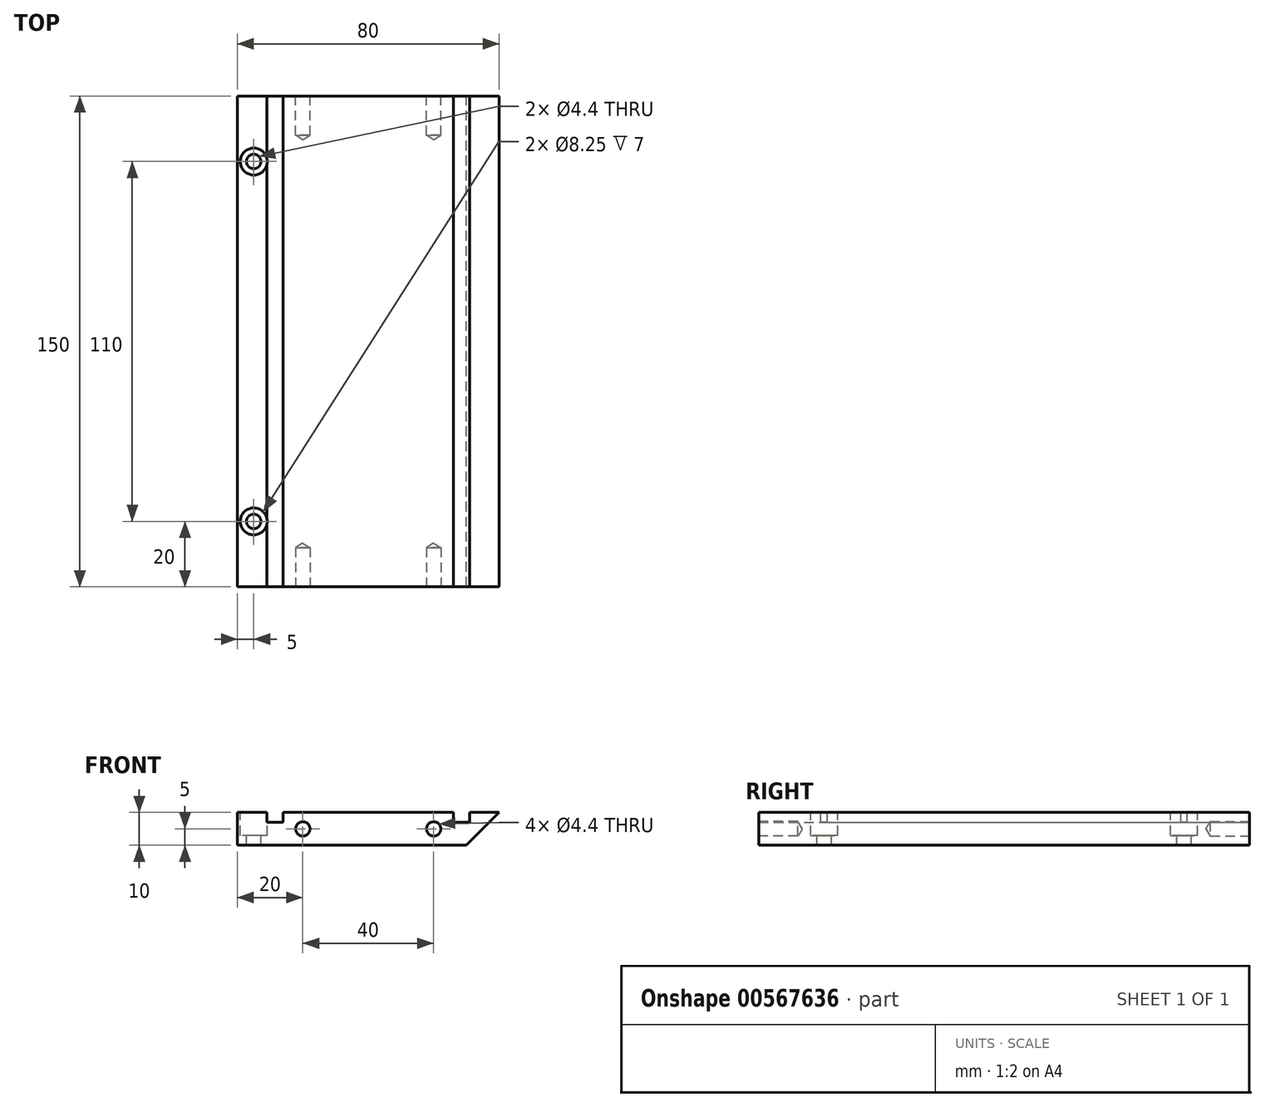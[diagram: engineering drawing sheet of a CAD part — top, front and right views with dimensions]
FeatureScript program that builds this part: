
annotation { "Feature Type Name" : "Feature", "Feature Type Description" : "" }
export const myFeature = defineFeature(function(context is Context, id is Id, definition is map)
    precondition{}
    {
        {
            var Q0;
            Q0=qCreatedBy(makeId("Front.planeOp"),FACE);
            var sketch = newSketch(context, id + "F0", { "sketchPlane" : qUnion([Q0])});
            skLineSegment(sketch, "E0.left", {"start": v(0, 0) * mm, "end": v(0, 10) * mm});
            skLineSegment(sketch, "E1", {"start": v(0, 10) * mm, "end": v(80, 10) * mm});
            skLineSegment(sketch, "E2", {"start": v(80, 10) * mm, "end": v(70, 0) * mm});
            skLineSegment(sketch, "E3", {"start": v(70, 0) * mm, "end": v(0, 0) * mm});
            skSolve(sketch);
        }
        {
            var Q0;
            Q0 = qSketchRegion(id + "F0", true);
            extrude(context, id + "F1", {"entities" : qUnion([Q0]), "depth" : 150 * mm, "offsetDistance" : 25 * mm});
        }
        {
            var Q0;
            Q0=makeQuery(id+"F1.opExtrude","CAP_FACE",FACE,{"disambiguationData":[OSD([sQuery(id+"F0.wireOp",EDGE,"E0.bottom"),sQuery(id+"F0.wireOp",EDGE,"E0.top"),sQuery(id+"F0.wireOp",EDGE,"E0.left"),sQuery(id+"F0.wireOp",EDGE,"E0.right")])],"isStart":false});
            var sketch = newSketch(context, id + "F2", { "sketchPlane" : qUnion([Q0])});
            skLineSegment(sketch, "E4", {"start": v(0, 5) * mm, "end": v(20, 5) * mm});
            skLineSegment(sketch, "E5", {"start": v(20, 5) * mm, "end": v(20, 10) * mm});
            skLineSegment(sketch, "E6", {"start": v(60, 10) * mm, "end": v(60, 5) * mm});
            skSolve(sketch);
        }
        {
            var Q0;
            Q0=sQuery(id+"F2.wireOp",VERTEX,"E5.start");
            var Q1;
            Q1=sQuery(id+"F2.wireOp",VERTEX,"E6.end");
            var Q2;
            Q2=makeQuery(id+"F1.opExtrude","SWEPT_BODY",BODY,{"disambiguationData":[OSD([sQuery(id+"F0.wireOp",EDGE,"E0.bottom"),sQuery(id+"F0.wireOp",EDGE,"E0.top"),sQuery(id+"F0.wireOp",EDGE,"E0.left"),sQuery(id+"F0.wireOp",EDGE,"E0.right")])]});
            hole(context, id + "F3", {"style" : HoleStyle.SIMPLE, "endStyle" : HoleEndStyle.BLIND, "standardTappedOrClearance" : lookupTablePath({ "standard" : "ISO", "fit" : "Normal", "size" : "M4", "type" : "Clearance" }), "standardBlindInLast" : lookupTablePath({ "fit" : "Standard", "standard" : "ISO", "size" : "M4", "type" : "Clearance" }), "holeDiameter" : 4.4 * mm, "holeDepth" : 12 * mm, "isTappedThrough" : true, "tappedDepth" : 12 * mm, "tapClearance" : 3, "locations" : qUnion([Q0, Q1]), "scope" : qUnion([Q2])});
        }
        {
            var Q0;
            Q0=makeQuery(id+"F1.opExtrude","CAP_FACE",FACE,{"disambiguationData":[OSD([sQuery(id+"F0.wireOp",EDGE,"E0.bottom"),sQuery(id+"F0.wireOp",EDGE,"E0.top"),sQuery(id+"F0.wireOp",EDGE,"E0.left"),sQuery(id+"F0.wireOp",EDGE,"E0.right")])],"isStart":true});
            var sketch = newSketch(context, id + "F4", { "sketchPlane" : qUnion([Q0])});
            skLineSegment(sketch, "E7", {"start": v(-60, 10) * mm, "end": v(-60, 5) * mm});
            skLineSegment(sketch, "E8", {"start": v(-20, 10) * mm, "end": v(-20, 5) * mm});
            skSolve(sketch);
        }
        {
            var Q0;
            Q0=sQuery(id+"F4.wireOp",VERTEX,"E7.end");
            var Q1;
            Q1=sQuery(id+"F4.wireOp",VERTEX,"E8.end");
            var Q2;
            Q2=makeQuery(id+"F1.opExtrude","SWEPT_BODY",BODY,{"disambiguationData":[OSD([sQuery(id+"F0.wireOp",EDGE,"E0.bottom"),sQuery(id+"F0.wireOp",EDGE,"E0.top"),sQuery(id+"F0.wireOp",EDGE,"E0.left"),sQuery(id+"F0.wireOp",EDGE,"E0.right")])]});
            hole(context, id + "F5", {"style" : HoleStyle.SIMPLE, "endStyle" : HoleEndStyle.BLIND, "standardTappedOrClearance" : lookupTablePath({ "standard" : "ISO", "fit" : "Normal", "size" : "M4", "type" : "Clearance" }), "standardBlindInLast" : lookupTablePath({ "fit" : "Standard", "standard" : "ISO", "size" : "M4", "type" : "Clearance" }), "holeDiameter" : 4.4 * mm, "holeDepth" : 12 * mm, "isTappedThrough" : true, "tappedDepth" : 12 * mm, "tapClearance" : 3, "locations" : qUnion([Q0, Q1]), "scope" : qUnion([Q2])});
        }
        {
            var Q0;
            Q0=makeQuery(id+"F1.opExtrude","CAP_FACE",FACE,{"disambiguationData":[OSD([sQuery(id+"F0.wireOp",EDGE,"E0.bottom"),sQuery(id+"F0.wireOp",EDGE,"E0.top"),sQuery(id+"F0.wireOp",EDGE,"E0.left"),sQuery(id+"F0.wireOp",EDGE,"E0.right")])],"isStart":true});
            var sketch = newSketch(context, id + "F6", { "sketchPlane" : qUnion([Q0])});
            skLineSegment(sketch, "E9.bottom", {"start": v(-71, 10) * mm, "end": v(-66, 10) * mm});
            skLineSegment(sketch, "E9.top", {"start": v(-71, 7) * mm, "end": v(-66, 7) * mm});
            skLineSegment(sketch, "E9.left", {"start": v(-71, 10) * mm, "end": v(-71, 7) * mm});
            skLineSegment(sketch, "E9.right", {"start": v(-66, 10) * mm, "end": v(-66, 7) * mm});
            skLineSegment(sketch, "E10.bottom", {"start": v(-14, 10) * mm, "end": v(-9, 10) * mm});
            skLineSegment(sketch, "E10.top", {"start": v(-14, 7) * mm, "end": v(-9, 7) * mm});
            skLineSegment(sketch, "E10.left", {"start": v(-14, 10) * mm, "end": v(-14, 7) * mm});
            skLineSegment(sketch, "E10.right", {"start": v(-9, 10) * mm, "end": v(-9, 7) * mm});
            skSolve(sketch);
        }
        {
            var Q0;
            Q0 = qSketchRegion(id + "F6", true);
            extrude(context, id + "F7", {"entities" : qUnion([Q0]), "operationType" : NewBodyOperationType.REMOVE, "endBound" : BoundingType.UP_TO_NEXT, "oppositeDirection" : true, "depth" : 25 * mm, "offsetDistance" : 25 * mm});
        }
        {
            var Q0;
            {var subQ0=sQuery(id+"F0.wireOp",EDGE,"E0.left");var subQ3=sQuery(id+"F0.wireOp",EDGE,"E1");Q0=makeQuery(id+"F7.boolean.opBoolean","SPLIT",FACE,{"disambiguationData":[TD([makeQuery(id+"F1.opExtrude","SWEPT_FACE",FACE,{"disambiguationData":[OSD([subQ0])]})])],"derivedFrom":makeQuery(id+"F1.opExtrude","SWEPT_FACE",FACE,{"disambiguationData":[OSD([subQ3])]})});}
            var sketch = newSketch(context, id + "F8", { "sketchPlane" : qUnion([Q0])});
            skLineSegment(sketch, "E11", {"start": v(5, -150) * mm, "end": v(5, -130) * mm});
            skLineSegment(sketch, "E12", {"start": v(5, 0) * mm, "end": v(5, -20) * mm});
            skSolve(sketch);
        }
        {
            var Q0;
            Q0=sQuery(id+"F8.wireOp",VERTEX,"E11.end");
            var Q1;
            Q1=sQuery(id+"F8.wireOp",VERTEX,"E12.end");
            var Q2;
            Q2=makeQuery(id+"F1.opExtrude","SWEPT_BODY",BODY,{"disambiguationData":[OSD([sQuery(id+"F0.wireOp",EDGE,"E0.left"),sQuery(id+"F0.wireOp",EDGE,"E1"),sQuery(id+"F0.wireOp",EDGE,"E2"),sQuery(id+"F0.wireOp",EDGE,"E3")])]});
            hole(context, id + "F9", {"style" : HoleStyle.C_BORE, "endStyle" : HoleEndStyle.BLIND, "standardTappedOrClearance" : lookupTablePath({ "standard" : "ISO", "fit" : "Normal", "size" : "M4", "type" : "Clearance" }), "standardBlindInLast" : lookupTablePath({ "fit" : "Standard", "standard" : "ISO", "size" : "M4", "type" : "Clearance" }), "holeDiameter" : 4.4 * mm, "cBoreDiameter" : 8.25 * mm, "cBoreDepth" : 4 * mm, "holeDepth" : 14.1 * mm, "isTappedThrough" : true, "tappedDepth" : 12 * mm, "tapClearance" : 3, "locations" : qUnion([Q0, Q1]), "scope" : qUnion([Q2])});
        }
    });
